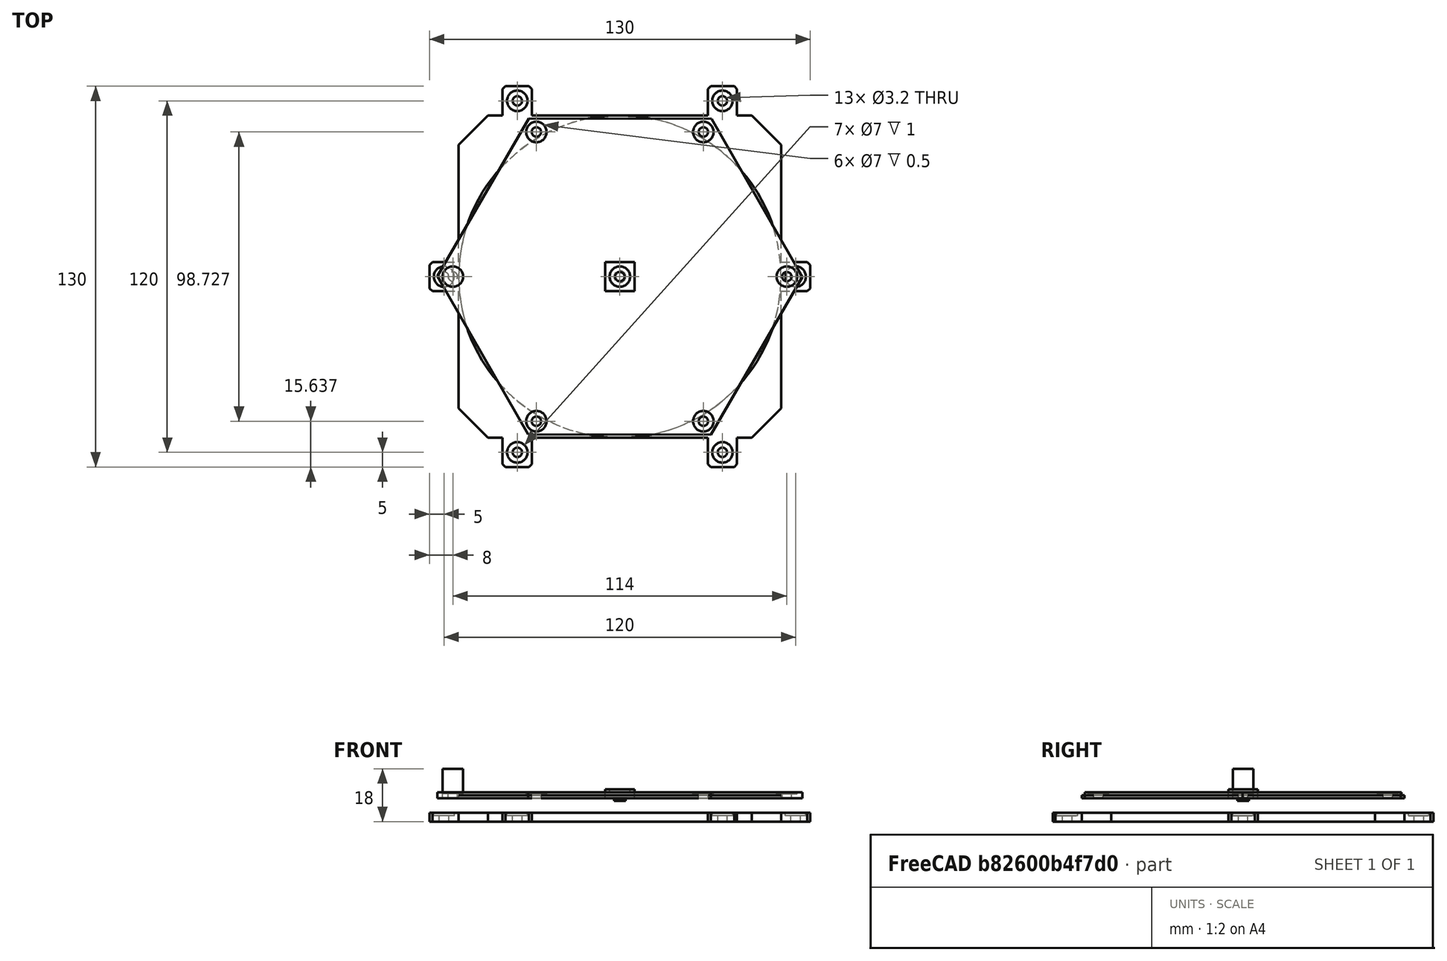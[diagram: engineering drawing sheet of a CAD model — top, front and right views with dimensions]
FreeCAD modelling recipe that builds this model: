
FCSTD DOCUMENT  (FreeCAD 0.18R16146 (Git))
Label: ps3-fan-cover
License: All rights reserved
LicenseURL: http://en.wikipedia.org/wiki/All_rights_reserved
objects: Part::Feature×19, Part::Cylinder×5, Part::Cut×4, Part::MultiFuse×3, Part::Box×2, Part::Chamfer×2
note: 35 computed .brp shape members not serialized (recipe doc carries the construction recipe); baked Part::Feature solids carry a one-line shape summary decoded from their .brp

FEATURE [Part::Box] Box  label="Cube"
  AttacherType = Attacher::AttachEngine3D
  Height = 3
  Length = 110
  Placement = pos=(-55,-55,0) rot=(0,0,1;0rad)
  Width = 110
FEATURE [Part::Box] Box001  label="Cube001"
  AttacherType = Attacher::AttachEngine3D
  Height = 3
  Length = 10
  Placement = pos=(-5,-5,0) rot=(0,0,1;0rad)
  Width = 10
FEATURE [Part::Cylinder] Cylinder
  Angle = 360
  AttacherType = Attacher::AttachEngine3D
  Height = 10
  Placement = pos=(0,0,2) rot=(0,0,1;0rad)
  Radius = 3.5
FEATURE [Part::Cut] Cut
  Base = -> Box001
  Tool = -> Cylinder
FEATURE [Part::Cylinder] Cylinder001
  Angle = 360
  AttacherType = Attacher::AttachEngine3D
  Height = 10
  Radius = 1.6
FEATURE [Part::Cut] Cut001  label="screw-hole"
  Base = -> Cut
  Tool = -> Cylinder001
FEATURE [Part::Feature] Cut001001  label="screw-hole001"
  Placement = pos=(-35,60,0) rot=(0,0,1;0rad)
  shape: bbox 10 x 10 x 3 mm, 9 faces (baked)
FEATURE [Part::Feature] Cut001002  label="screw-hole002"
  Placement = pos=(60,0,0) rot=(0,0,1;0rad)
  shape: bbox 10 x 10 x 3 mm, 9 faces (baked)
FEATURE [Part::Feature] Cut001003  label="screw-hole003"
  Placement = pos=(-60,0,0) rot=(0,0,1;0rad)
  shape: bbox 10 x 10 x 3 mm, 9 faces (baked)
FEATURE [Part::Feature] Cut001004  label="screw-hole004"
  Placement = pos=(-35,-60,0) rot=(0,0,1;0rad)
  shape: bbox 10 x 10 x 3 mm, 9 faces (baked)
FEATURE [Part::Feature] Cut001005  label="screw-hole005"
  Placement = pos=(35,60,0) rot=(0,0,1;0rad)
  shape: bbox 10 x 10 x 3 mm, 9 faces (baked)
FEATURE [Part::Feature] Cut001006  label="screw-hole006"
  Placement = pos=(35,-60,0) rot=(0,0,1;0rad)
  shape: bbox 10 x 10 x 3 mm, 9 faces (baked)
FEATURE [Part::MultiFuse] Fusion
  Shapes = -> [Cut001006,Cut001005,Cut001004,Cut001003,Cut001002,Cut001001,Box]
FEATURE [Part::Chamfer] Chamfer
  Base = -> Fusion
  Edges = 4 edges r=10: [Edge4,Edge42,Edge55,Edge58]
FEATURE [Part::Chamfer] Chamfer001
  Base = -> Chamfer
  Edges = 12 edges r=1: [Edge28,Edge90,Edge113,Edge114,Edge117,Edge118,Edge119,Edge122,Edge125,Edge126,Edge129,Edge130]
  Placement = pos=(0,0,-8) rot=(0,0,1;0rad)
FEATURE [Part::Cylinder] Cylinder002
  Angle = 360
  AttacherType = Attacher::AttachEngine3D
  Height = 1
  Placement = pos=(0,0,-1) rot=(0,0,1;0rad)
  Radius = 2
FEATURE [Part::Cylinder] Cylinder003
  Angle = 360
  AttacherType = Attacher::AttachEngine3D
  Height = 1
  Radius = 55
FEATURE [Part::Cylinder] Cylinder004
  Angle = 360
  AttacherType = Attacher::AttachEngine3D
  Height = 10
  Placement = pos=(-57,0,0) rot=(0,0,1;0rad)
  Radius = 3.5
FEATURE [Part::Feature] Cylinder004001  label="Cylinder005"
  Placement = pos=(0,0,0) rot=(0,0,1;5.23599rad)
  shape: bbox 3.2 x 3.2 x 10 mm, 3 faces (baked)
FEATURE [Part::Feature] Cylinder004002  label="Cylinder006"
  Placement = pos=(0,0,0) rot=(0,0,1;4.18879rad)
  shape: bbox 3.2 x 3.2 x 10 mm, 3 faces (baked)
FEATURE [Part::Feature] Cylinder004003  label="Cylinder007"
  Placement = pos=(0,0,0) rot=(0,0,1;3.14159rad)
  shape: bbox 3.2 x 3.2 x 10 mm, 3 faces (baked)
FEATURE [Part::Feature] Cylinder004004  label="Cylinder008"
  Placement = pos=(0,0,0) rot=(0,0,1;2.0944rad)
  shape: bbox 3.2 x 3.2 x 10 mm, 3 faces (baked)
FEATURE [Part::Feature] Cylinder004005  label="Cylinder009"
  Placement = pos=(0,0,0) rot=(0,0,1;1.0472rad)
  shape: bbox 3.2 x 3.2 x 10 mm, 3 faces (baked)
FEATURE [Part::Feature] Cylinder004006  label="Cylinder010"
  shape: bbox 3.2 x 3.2 x 10 mm, 3 faces (baked)
FEATURE [Part::Feature] Body001
  shape: bbox 124.5 x 108 x 2 mm, 8 faces (baked)
FEATURE [Part::MultiFuse] Fusion001
  Shapes = -> [Cylinder004001,Cylinder004003,Cylinder004002,Cylinder004004,Cylinder004006,Cylinder004005]
FEATURE [Part::Cut] Cut001007
  Base = -> Body001
  Tool = -> Fusion001
FEATURE [Part::Feature] Cylinder004007  label="Cylinder011"
  shape: bbox 7 x 7 x 10 mm, 3 faces (baked)
FEATURE [Part::Feature] Cylinder004008  label="Cylinder012"
  Placement = pos=(0,0,0) rot=(0,0,1;5.23599rad)
  shape: bbox 7 x 7 x 10 mm, 3 faces (baked)
FEATURE [Part::Feature] Cylinder004009  label="Cylinder013"
  Placement = pos=(0,0,0) rot=(0,0,1;4.18879rad)
  shape: bbox 7 x 7 x 10 mm, 3 faces (baked)
FEATURE [Part::Feature] Cylinder004010  label="Cylinder014"
  Placement = pos=(0,0,0) rot=(0,0,1;3.14159rad)
  shape: bbox 7 x 7 x 10 mm, 3 faces (baked)
FEATURE [Part::Feature] Cylinder004011  label="Cylinder015"
  Placement = pos=(0,0,0) rot=(0,0,1;2.0944rad)
  shape: bbox 7 x 7 x 10 mm, 3 faces (baked)
FEATURE [Part::Feature] Cylinder004012  label="Cylinder016"
  Placement = pos=(0,0,0) rot=(0,0,1;1.0472rad)
  shape: bbox 7 x 7 x 10 mm, 3 faces (baked)
FEATURE [Part::MultiFuse] Fusion002
  Placement = pos=(0,0,1.5) rot=(0,0,1;0rad)
  Shapes = -> [Cylinder004007,Cylinder004011,Cylinder004009,Cylinder004008,Cylinder004010,Cylinder004012]
FEATURE [Part::Cut] Cut001008
  Base = -> Cut001007
  Tool = -> Fusion002
